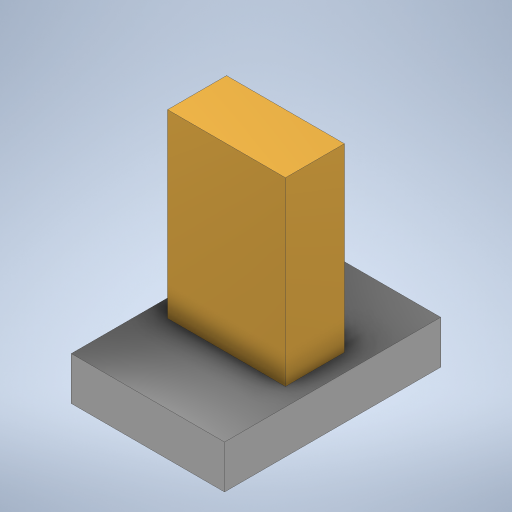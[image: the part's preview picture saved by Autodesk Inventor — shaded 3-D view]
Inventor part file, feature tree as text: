
AUTODESK INVENTOR PART (.ipt)
format: ipt  version: 2023 (Build 270158000, 158)  size: 230,912 bytes
history: native  units: in
note: dims shown in document units (in); Inventor stores cm internally (conversion verified against a paired STEP export)
features: extrude x2, sketch x2
ambient origin geometry x8: Origin, YZ Plane, XZ Plane, XY Plane, X Axis, Y Axis, Z Axis, Center Point
bodies: Solid1 (feature_tree)
feature tree (4):
  extrude  "Extrusion1"  Depth=0.39in
  extrude  "Extrusion2"  Depth=0.15in
  sketch  "Sketch1"  dims[d0=0.55in d1=0.39in]
  sketch  "Sketch2"  dims[d2=0.11in d3=0.0in d4=0.15in d5=0.3in d6=0.46in d7=0.0in]
